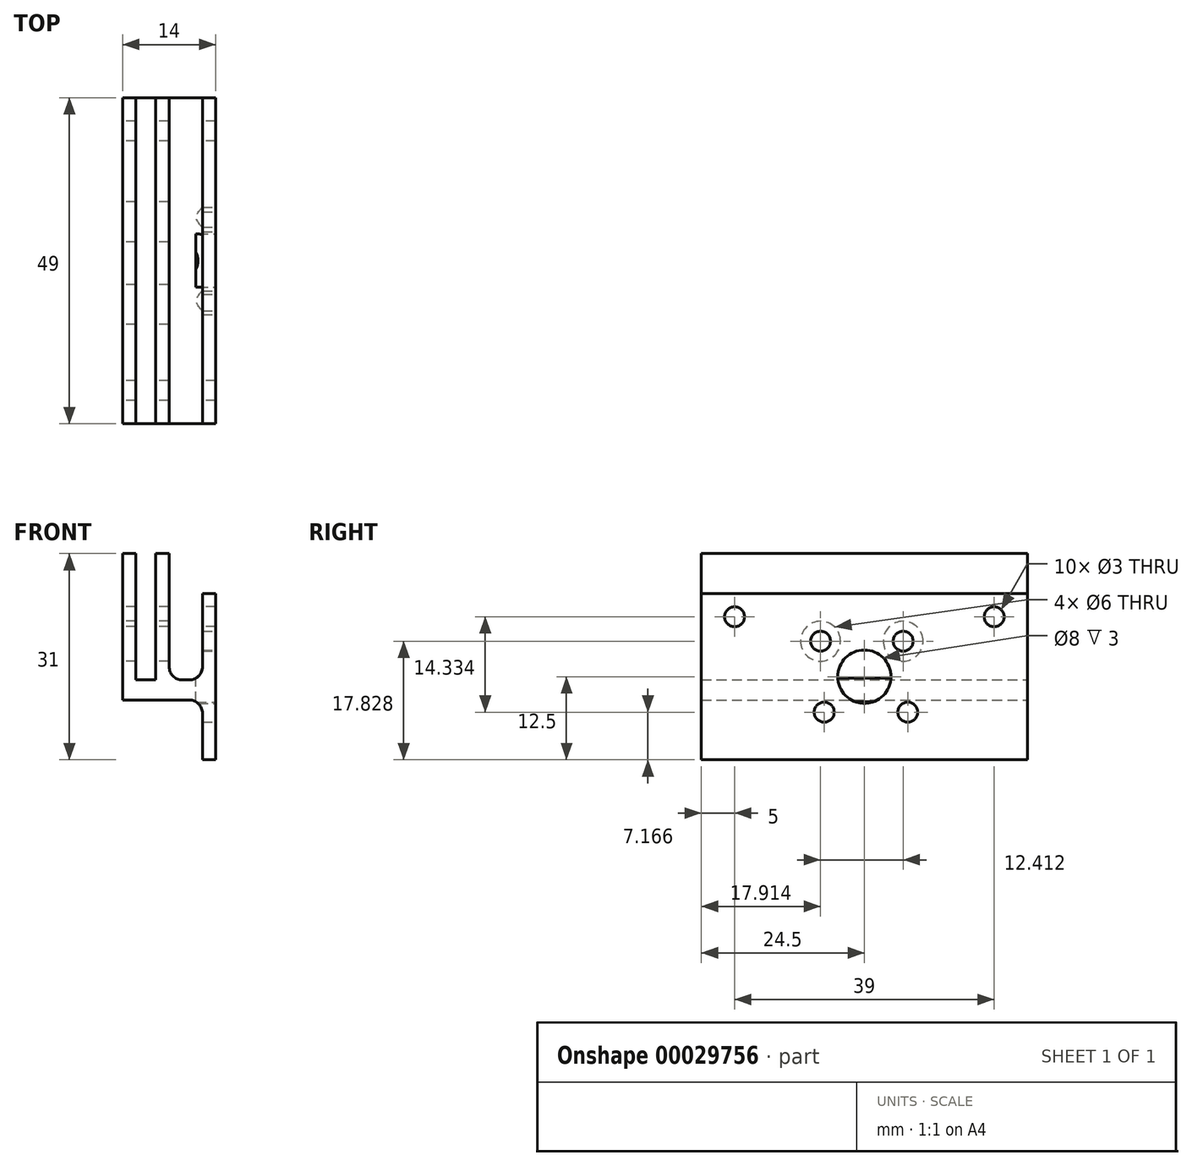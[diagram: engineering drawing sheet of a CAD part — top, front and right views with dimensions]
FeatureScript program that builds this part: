
annotation { "Feature Type Name" : "Feature", "Feature Type Description" : "" }
export const myFeature = defineFeature(function(context is Context, id is Id, definition is map)
    precondition{}
    {
        {
            var Q0;
            Q0=qCreatedBy(makeId("Front.planeOp"),FACE);
            var sketch = newSketch(context, id + "F0", { "sketchPlane" : qUnion([Q0])});
            skLineSegment(sketch, "E0.bottom", {"start": v(0, 0) * mm, "end": v(2, 0) * mm});
            skLineSegment(sketch, "E0.top", {"start": v(0, 22) * mm, "end": v(2, 22) * mm});
            skLineSegment(sketch, "E0.left", {"start": v(0, 0) * mm, "end": v(0, 22) * mm});
            skLineSegment(sketch, "E0.right", {"start": v(2, 3) * mm, "end": v(2, 22) * mm});
            skLineSegment(sketch, "E1", {"start": v(2, 0) * mm, "end": v(12, 0) * mm});
            skLineSegment(sketch, "E2", {"start": v(14, 0) * mm, "end": v(14, 16) * mm});
            skLineSegment(sketch, "E3", {"start": v(14, 16) * mm, "end": v(12, 16) * mm});
            skLineSegment(sketch, "E4", {"start": v(12, 16) * mm, "end": v(12, 3) * mm});
            skLineSegment(sketch, "E5", {"start": v(12, 3) * mm, "end": v(7, 3) * mm});
            skLineSegment(sketch, "E6", {"start": v(7, 22) * mm, "end": v(5, 22) * mm});
            skLineSegment(sketch, "E7", {"start": v(5, 22) * mm, "end": v(5, 3) * mm});
            skLineSegment(sketch, "E8", {"start": v(5, 3) * mm, "end": v(2, 3) * mm});
            skLineSegment(sketch, "E9", {"start": v(7, 22) * mm, "end": v(7, 3) * mm});
            skLineSegment(sketch, "E10", {"start": v(12, 0) * mm, "end": v(12, -9) * mm});
            skLineSegment(sketch, "E11", {"start": v(12, -9) * mm, "end": v(14, -9) * mm});
            skLineSegment(sketch, "E12", {"start": v(14, -9) * mm, "end": v(14, 0) * mm});
            skSolve(sketch);
        }
        {
            var Q0;
            Q0=qSketchRegion(id+"F0",true);
            extrude(context, id + "F1", {"entities" : qUnion([Q0]), "depth" : 49 * mm});
        }
        {
            var Q0;
            Q0=makeQuery(id+"F1.opExtrude","SWEPT_FACE",FACE,{"disambiguationData":[OSD([sQuery(id+"F0.wireOp",EDGE,"E2"),sQuery(id+"F0.wireOp",EDGE,"E12")])]});
            var sketch = newSketch(context, id + "F2", { "sketchPlane" : qUnion([Q0])});
            skCircle(sketch, "E13", {"center": v(-18.67, 8.83) * mm, "radius": 1.5 * mm});
            skCircle(sketch, "E14", {"center": v(-17.98, -1.83) * mm, "radius": 1.5 * mm});
            skCircle(sketch, "E15", {"center": v(-30.54, -1.83) * mm, "radius": 1.5 * mm});
            skCircle(sketch, "E16", {"center": v(-31.09, 8.83) * mm, "radius": 1.5 * mm});
            skCircle(sketch, "E17", {"center": v(-24.5, 3.5) * mm, "radius": 4 * mm});
            skLineSegment(sketch, "E18", {"start": v(-14.08, -1.83) * mm, "end": v(-39.92, -1.83) * mm, "construction": true});
            skLineSegment(sketch, "E19", {"start": v(-37.86, 8.83) * mm, "end": v(-11.14, 8.83) * mm, "construction": true});
            skLineSegment(sketch, "E20", {"start": v(-17.98, -1.83) * mm, "end": v(-37.3, 13.88) * mm, "construction": true});
            skLineSegment(sketch, "E21", {"start": v(-16.53, 10.8) * mm, "end": v(-35.08, -5.93) * mm, "construction": true});
            skSolve(sketch);
        }
        {
            var Q0;
            Q0=makeQuery(id+"F2.imprint","IMPRINT",FACE,{"disambiguationData":[TD([[makeQuery(id+"F2.imprint","IMPRINT",EDGE,{"derivedFrom":sQuery(id+"F2.wireOp",EDGE,"E16")}),1.0]])]});
            var Q1;
            Q1=makeQuery(id+"F2.imprint","IMPRINT",FACE,{"disambiguationData":[TD([[makeQuery(id+"F2.imprint","IMPRINT",EDGE,{"derivedFrom":sQuery(id+"F2.wireOp",EDGE,"E13")}),1.0]])]});
            var Q2;
            Q2=makeQuery(id+"F2.imprint","IMPRINT",FACE,{"disambiguationData":[TD([[makeQuery(id+"F2.imprint","IMPRINT",EDGE,{"derivedFrom":sQuery(id+"F2.wireOp",EDGE,"E14")}),1.0]])]});
            var Q3;
            Q3=makeQuery(id+"F2.imprint","IMPRINT",FACE,{"disambiguationData":[TD([[makeQuery(id+"F2.imprint","IMPRINT",EDGE,{"derivedFrom":sQuery(id+"F2.wireOp",EDGE,"E15")}),1.0]])]});
            var Q4;
            Q4=makeQuery(id+"F1.opExtrude","SWEPT_FACE",FACE,{"disambiguationData":[OSD([sQuery(id+"F0.wireOp",EDGE,"E9")])]});
            extrude(context, id + "F3", {"entities" : qUnion([Q0, Q1, Q2, Q3]), "operationType" : NewBodyOperationType.REMOVE, "oppositeDirection" : true, "endBoundEntityFace" : qUnion([Q4]), "depth" : 25 * mm});
        }
        {
            var Q0;
            Q0=makeQuery(id+"F1.opExtrude","SWEPT_EDGE",EDGE,{"disambiguationData":[OSD([sQuery(id+"F0.wireOp",EDGE,"E1"),sQuery(id+"F0.wireOp",EDGE,"E10")])]});
            var Q1;
            Q1=makeQuery(id+"F1.opExtrude","SWEPT_EDGE",EDGE,{"disambiguationData":[OSD([sQuery(id+"F0.wireOp",EDGE,"E4"),sQuery(id+"F0.wireOp",EDGE,"E5")])]});
            var Q2;
            Q2=makeQuery(id+"F1.opExtrude","SWEPT_EDGE",EDGE,{"disambiguationData":[OSD([sQuery(id+"F0.wireOp",EDGE,"E5"),sQuery(id+"F0.wireOp",EDGE,"E9")])]});
            fillet(context, id + "F4", {"entities" : qUnion([Q0, Q1, Q2]), "radius" : 2 * mm, "tangentPropagation" : true, "allowEdgeOverflow" : false});
        }
        {
            var Q0;
            Q0=makeQuery(id+"F1.opExtrude","SWEPT_FACE",FACE,{"disambiguationData":[OSD([sQuery(id+"F0.wireOp",EDGE,"E0.left")])]});
            var sketch = newSketch(context, id + "F5", { "sketchPlane" : qUnion([Q0])});
            skCircle(sketch, "E22", {"center": v(44, 12.5) * mm, "radius": 1.5 * mm});
            skPoint(sketch, "E22.centerSnap0", {"position": v(49, 12.5) * mm});
            skCircle(sketch, "E23", {"center": v(5, 12.5) * mm, "radius": 1.5 * mm});
            skPoint(sketch, "E23.centerSnap0", {"position": v(0.03, 12.5) * mm});
            skSolve(sketch);
        }
        {
            var Q0;
            Q0=makeQuery(id+"F2.imprint","IMPRINT",FACE,{"disambiguationData":[TD([[makeQuery(id+"F2.imprint","IMPRINT",EDGE,{"derivedFrom":sQuery(id+"F2.wireOp",EDGE,"E16")}),1.0]])]});
            var Q1;
            Q1=makeQuery(id+"F2.imprint","IMPRINT",FACE,{"disambiguationData":[TD([[makeQuery(id+"F2.imprint","IMPRINT",EDGE,{"derivedFrom":sQuery(id+"F2.wireOp",EDGE,"E13")}),1.0]])]});
            var Q2;
            Q2=makeQuery(id+"F2.imprint","IMPRINT",FACE,{"disambiguationData":[TD([[makeQuery(id+"F2.imprint","IMPRINT",EDGE,{"derivedFrom":sQuery(id+"F2.wireOp",EDGE,"E14")}),1.0]])]});
            var Q3;
            Q3=makeQuery(id+"F2.imprint","IMPRINT",FACE,{"disambiguationData":[TD([[makeQuery(id+"F2.imprint","IMPRINT",EDGE,{"derivedFrom":sQuery(id+"F2.wireOp",EDGE,"E15")}),1.0]])]});
            var Q4;
            Q4=makeQuery(id+"F1.opExtrude","SWEPT_FACE",FACE,{"disambiguationData":[OSD([sQuery(id+"F0.wireOp",EDGE,"E0.right")])]});
            extrude(context, id + "F6", {"entities" : qUnion([Q0, Q1, Q2, Q3]), "operationType" : NewBodyOperationType.REMOVE, "oppositeDirection" : true, "endBoundEntityFace" : qUnion([Q4]), "depth" : 25 * mm});
        }
        {
            var Q0;
            Q0=qSketchRegion(id+"F2",true);
            var Q1;
            Q1=makeQuery(id+"F1.opExtrude","SWEPT_FACE",FACE,{"disambiguationData":[OSD([sQuery(id+"F0.wireOp",EDGE,"E4")])]});
            extrude(context, id + "F7", {"entities" : qUnion([Q0]), "operationType" : NewBodyOperationType.REMOVE, "oppositeDirection" : true, "endBoundEntityFace" : qUnion([Q1]), "depth" : 3 * mm});
        }
        {
            var Q0;
            Q0=qSketchRegion(id+"F5",true);
            extrude(context, id + "F8", {"entities" : qUnion([Q0]), "operationType" : NewBodyOperationType.REMOVE, "oppositeDirection" : true, "depth" : 25 * mm});
        }
        {
            var Q0;
            Q0=makeQuery(id+"F1.opExtrude","SWEPT_FACE",FACE,{"disambiguationData":[OSD([sQuery(id+"F0.wireOp",EDGE,"E0.left")])]});
            var sketch = newSketch(context, id + "F9", { "sketchPlane" : qUnion([Q0])});
            skCircle(sketch, "E24", {"center": v(31.09, 8.83) * mm, "radius": 3 * mm});
            skCircle(sketch, "E25", {"center": v(18.67, 8.83) * mm, "radius": 3 * mm});
            skSolve(sketch);
        }
        {
            var Q0;
            Q0=makeQuery(id+"F9.imprint","IMPRINT",FACE,{"disambiguationData":[TD([[makeQuery(id+"F9.imprint","IMPRINT",EDGE,{"derivedFrom":sQuery(id+"F9.wireOp",EDGE,"E24")}),1.0]])]});
            var Q1;
            Q1=makeQuery(id+"F9.imprint","IMPRINT",FACE,{"disambiguationData":[TD([[makeQuery(id+"F9.imprint","IMPRINT",EDGE,{"derivedFrom":sQuery(id+"F9.wireOp",EDGE,"E25")}),1.0]])]});
            var Q2;
            Q2=makeQuery(id+"F1.opExtrude","SWEPT_FACE",FACE,{"disambiguationData":[OSD([sQuery(id+"F0.wireOp",EDGE,"E9")])]});
            extrude(context, id + "F10", {"entities" : qUnion([Q0, Q1]), "operationType" : NewBodyOperationType.REMOVE, "endBound" : BoundingType.UP_TO_SURFACE, "oppositeDirection" : true, "endBoundEntityFace" : qUnion([Q2]), "depth" : 25 * mm});
        }
    });
